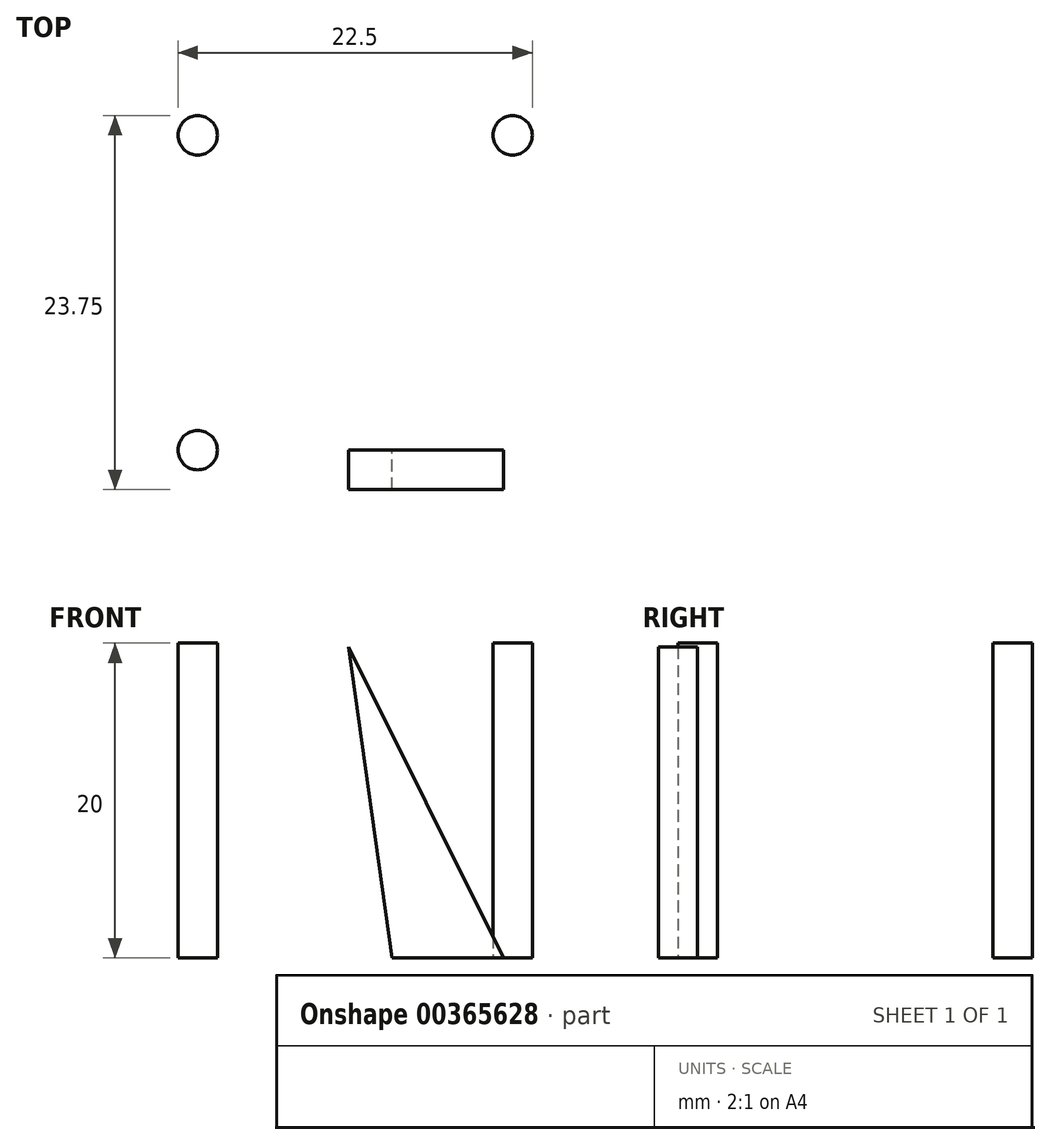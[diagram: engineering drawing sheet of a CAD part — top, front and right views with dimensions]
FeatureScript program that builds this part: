
annotation { "Feature Type Name" : "Feature", "Feature Type Description" : "" }
export const myFeature = defineFeature(function(context is Context, id is Id, definition is map)
    precondition{}
    {
        {
            var Q0;
            Q0=qCreatedBy(makeId("Top.planeOp"),FACE);
            var sketch = newSketch(context, id + "F0", { "sketchPlane" : qUnion([Q0])});
            skCircle(sketch, "E0", {"center": v(0, 20) * mm, "radius": 1.25 * mm});
            skCircle(sketch, "E1", {"center": v(0, 0) * mm, "radius": 1.25 * mm});
            skCircle(sketch, "E2", {"center": v(20, 20) * mm, "radius": 1.25 * mm});
            skSolve(sketch);
        }
        {
            var Q0;
            Q0 = qSketchRegion(id + "F0", true);
            extrude(context, id + "F1", {"entities" : qUnion([Q0]), "depth" : 20 * mm});
        }
        {
            var Q0;
            Q0=qCreatedBy(makeId("Front.planeOp"),FACE);
            var sketch = newSketch(context, id + "F2", { "sketchPlane" : qUnion([Q0])});
            skLineSegment(sketch, "E3", {"start": v(19.43, 0) * mm, "end": v(9.6, 19.74) * mm});
            skLineSegment(sketch, "E4", {"start": v(9.6, 19.74) * mm, "end": v(12.33, 0) * mm});
            skLineSegment(sketch, "E5", {"start": v(12.33, 0) * mm, "end": v(19.43, 0) * mm});
            skSolve(sketch);
        }
        {
            var Q0;
            Q0 = qSketchRegion(id + "F2", true);
            extrude(context, id + "F3", {"entities" : qUnion([Q0]), "depth" : 2.5 * mm});
        }
    });
